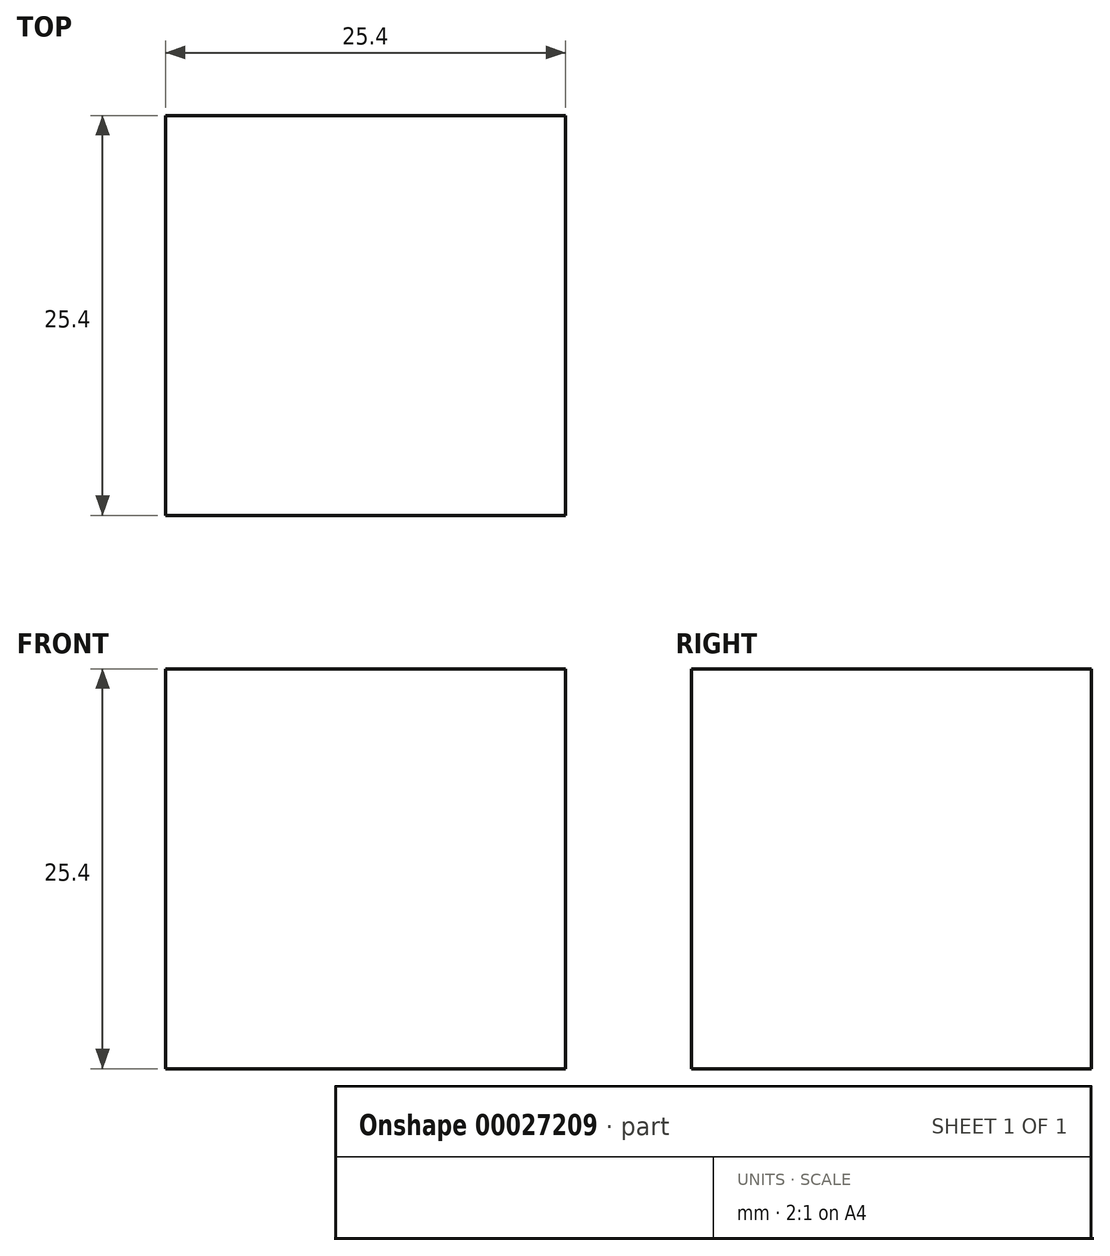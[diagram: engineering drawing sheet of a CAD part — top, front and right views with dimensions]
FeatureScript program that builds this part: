
annotation { "Feature Type Name" : "Feature", "Feature Type Description" : "" }
export const myFeature = defineFeature(function(context is Context, id is Id, definition is map)
    precondition{}
    {
        {
            var Q0;
            Q0=qCreatedBy(makeId("Front.planeOp"),FACE);
            var sketch = newSketch(context, id + "F0", { "sketchPlane" : qUnion([Q0])});
            skLineSegment(sketch, "E0.bottom", {"start": v(0, 0) * mm, "end": v(25.4, 0) * mm});
            skLineSegment(sketch, "E0.top", {"start": v(0, 25.4) * mm, "end": v(25.4, 25.4) * mm});
            skLineSegment(sketch, "E0.left", {"start": v(0, 0) * mm, "end": v(0, 25.4) * mm});
            skLineSegment(sketch, "E0.right", {"start": v(25.4, 0) * mm, "end": v(25.4, 25.4) * mm});
            skSolve(sketch);
        }
        {
            var Q0;
            Q0=makeQuery(id+"F0.imprint","IMPRINT",FACE,{"disambiguationData":[TD([[makeQuery(id+"F0.imprint","IMPRINT",EDGE,{"derivedFrom":sQuery(id+"F0.wireOp",EDGE,"E0.bottom")}),1.0]])]});
            extrude(context, id + "F1", {"entities" : qUnion([Q0]), "depth" : 25.4 * mm});
        }
    });
